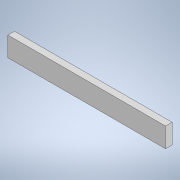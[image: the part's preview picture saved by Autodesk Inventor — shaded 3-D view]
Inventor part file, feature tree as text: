
AUTODESK INVENTOR PART (.ipt)
format: ipt  version: 2021 (Build 250183000, 183)  size: 99,328 bytes
history: native  units: in
note: dims shown in document units (in); Inventor stores cm internally (conversion verified against a paired STEP export)
features: extrude x1, sketch x1
ambient origin geometry x8: Origin, YZ Plane, XZ Plane, XY Plane, X Axis, Y Axis, Z Axis, Center Point
bodies: Solid1 (feature_tree)
feature tree (2):
  extrude  "Extrusion1"  Depth=0.375in
  sketch  "Sketch1"  dims[d0=3.0in d1=0.375in d2=0.125in d3=0.0in]
